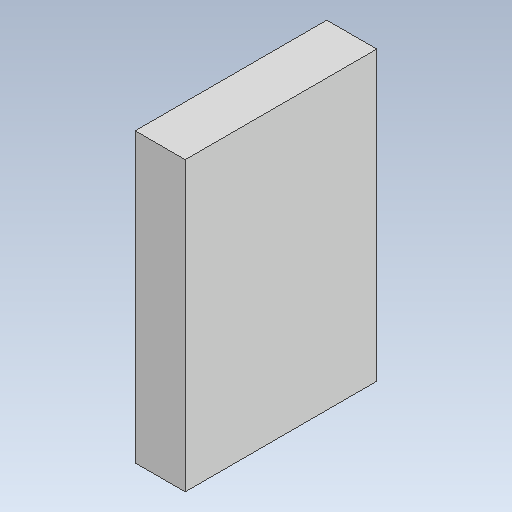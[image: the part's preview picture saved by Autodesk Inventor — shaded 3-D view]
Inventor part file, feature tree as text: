
AUTODESK INVENTOR PART (.ipt)
format: ipt  version: 2020 (Build 240168000, 168)  size: 112,128 bytes
history: native  units: mm
features: extrude x2, sketch x1
ambient origin geometry x8: Origin, YZ Plane, XZ Plane, XY Plane, X Axis, Y Axis, Z Axis, Center Point
bodies: Solid1 (feature_tree)
feature tree (3):
  extrude  "Extrusion1"  Depth=8.7mm
  extrude  "Extrusion2"  Depth=50.0mm TaperAngle=0.0deg
  sketch  "Sketch2"  dims[d0=33.3mm d1=8.7mm d2=50.0mm d3=0.0mm d4=2.5mm d5=2.9mm d6=1.5mm d7=2.9mm d8=10.0mm d9=0.0mm]
